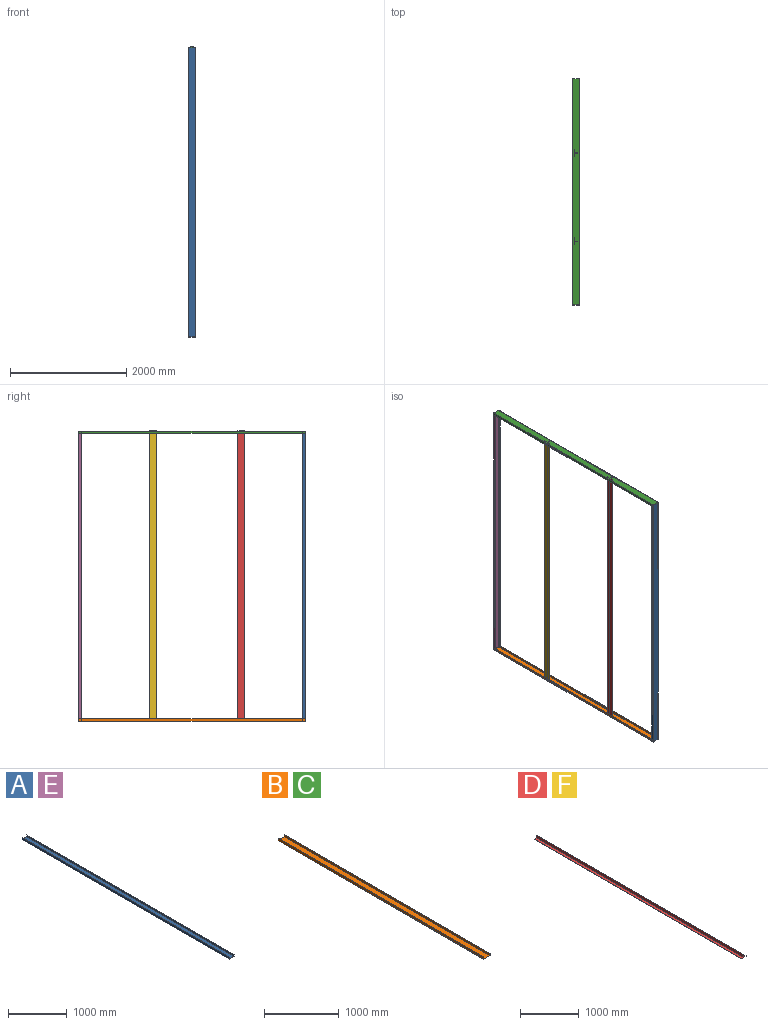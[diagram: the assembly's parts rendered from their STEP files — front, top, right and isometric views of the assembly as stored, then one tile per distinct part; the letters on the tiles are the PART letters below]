
ASSEMBLY  parts=6 mates=11
PART A: 10 faces, bbox 120x5000x40 mm
  f0: plane 5000x107.96mm, normal (0,0,1), area 539811.7mm2, adj f1,f7,f8,f9
  f1: plane 5000x34.05mm, normal (1,0,0.07), area 170705.5mm2, adj f0,f2,f8,f9
  f2: plane 5000x3.51mm, normal (0,0,1), area 17542mm2, adj f1,f3,f8,f9
  f3: plane 5000x40mm, normal (-1,0,0), area 200000mm2, adj f2,f4,f8,f9
  f4: plane 5000x120mm, normal (0,0,-1), area 600000mm2, adj f3,f5,f8,f9
  f5: plane 5000x40mm, normal (1,0,0), area 200000mm2, adj f4,f6,f8,f9
  f6: plane 5000x3.51mm, normal (0,0,1), area 17542mm2, adj f5,f7,f8,f9
  f7: plane 5000x34.05mm, normal (-1,0,0.07), area 170705.5mm2, adj f0,f6,f8,f9
  f8: plane 120x40mm, normal (0,-1,0), area 1038.5mm2, adj f0,f1,f2,f3,f4,f5,f6,f7
  f9: plane 120x40mm, normal (0,1,0), area 1038.5mm2, adj f0,f1,f2,f3,f4,f5,f6,f7
PART B: 10 faces, bbox 120x3900x40 mm
  f0: plane 3900x107.96mm, normal (0,0,1), area 421053.2mm2, adj f1,f7,f8,f9
  f1: plane 3900x34.05mm, normal (1,0,0.07), area 133150.3mm2, adj f0,f2,f8,f9
  f2: plane 3900x3.51mm, normal (0,0,1), area 13682.7mm2, adj f1,f3,f8,f9
  f3: plane 3900x40mm, normal (-1,0,0), area 156000mm2, adj f2,f4,f8,f9
  f4: plane 3900x120mm, normal (0,0,-1), area 468000mm2, adj f3,f5,f8,f9
  f5: plane 3900x40mm, normal (1,0,0), area 156000mm2, adj f4,f6,f8,f9
  f6: plane 3900x3.51mm, normal (0,0,1), area 13682.7mm2, adj f5,f7,f8,f9
  f7: plane 3900x34.05mm, normal (-1,0,0.07), area 133150.3mm2, adj f0,f6,f8,f9
  f8: plane 120x40mm, normal (0,-1,0), area 1038.5mm2, adj f0,f1,f2,f3,f4,f5,f6,f7
  f9: plane 120x40mm, normal (0,1,0), area 1038.5mm2, adj f0,f1,f2,f3,f4,f5,f6,f7
PART C: same geometry as B
PART D: 10 faces, bbox 120x5000x60 mm
  f0: plane 5000x58mm, normal (0,0,1), area 290000mm2, adj f1,f7,f8,f9
  f1: plane 5000x56mm, normal (1,0,0.02), area 280042.7mm2, adj f0,f2,f8,f9
  f2: plane 5000x2.05mm, normal (0,0,1), area 10225.2mm2, adj f1,f3,f8,f9
  f3: plane 5000x56mm, normal (-1,0,0.02), area 280042.7mm2, adj f2,f4,f8,f9
  f4: plane 5000x58mm, normal (0,0,1), area 290000mm2, adj f3,f5,f8,f9
  f5: plane 5000x4mm, normal (-1,0,0), area 20000mm2, adj f4,f6,f8,f9
  f6: plane 5000x120mm, normal (0,0,-1), area 600000mm2, adj f5,f7,f8,f9
  f7: plane 5000x4mm, normal (1,0,0), area 20000mm2, adj f0,f6,f8,f9
  f8: plane 120x60mm, normal (0,-1,0), area 649.3mm2, adj f0,f1,f2,f3,f4,f5,f6,f7
  f9: plane 120x60mm, normal (0,1,0), area 649.3mm2, adj f0,f1,f2,f3,f4,f5,f6,f7
PART E: same geometry as A
PART F: same geometry as D
PLACE A rot(axis=(-1,0,0),90deg) t=(-33.98,-2496.43,-1930)mm fixed
PLACE B t=(-33.98,1403.57,-1930)mm
PLACE C rot(axis=(0,1,0),180deg) t=(-33.98,1403.57,3070)mm
PLACE D rot(axis=(-0.58,0.58,-0.58),120deg) t=(-68.36,-1399.43,-1924.05)mm
PLACE E rot(axis=(1,0,0),90deg) t=(-33.98,1403.57,3070)mm
PLACE F rot(axis=(-0.58,0.58,-0.58),120deg) t=(-67.98,122.07,-1924.05)mm
MATE planar E.f4 <-> B.f9  axis (0,1,0) through (-33.98,1403.57,570)mm
MATE planar B.f4 <-> A.f9  axis (0,0,-1) through (-33.98,-546.43,-1930)mm
MATE planar B.f8 <-> A.f4  axis (0,-1,0) through (-33.98,-2496.43,-1921.24)mm
MATE planar E.f4 <-> C.f9  axis (0,1,0) through (-33.98,1403.57,570)mm
MATE planar F.f9 <-> B.f0  axis (0,0,-1) through (-63.98,124.07,-1924.05)mm
MATE planar C.f4 <-> E.f9  axis (0,0,1) through (-33.98,-546.43,3070)mm
MATE planar E.f8 <-> B.f4  axis (0,0,-1) through (20,1397.62,-1930)mm
MATE planar C.f3 <-> E.f5  axis (1,0,0) through (26.02,-546.43,3050)mm
MATE planar D.f9 <-> B.f0  axis (0,0,-1) through (-59.32,-1399.43,-1924.05)mm
MATE planar B.f5 <-> A.f5  axis (1,0,0) through (26.02,-546.43,-1910)mm
MATE planar E.f5 <-> B.f5  axis (1,0,0) through (26.02,1383.57,570)mm
